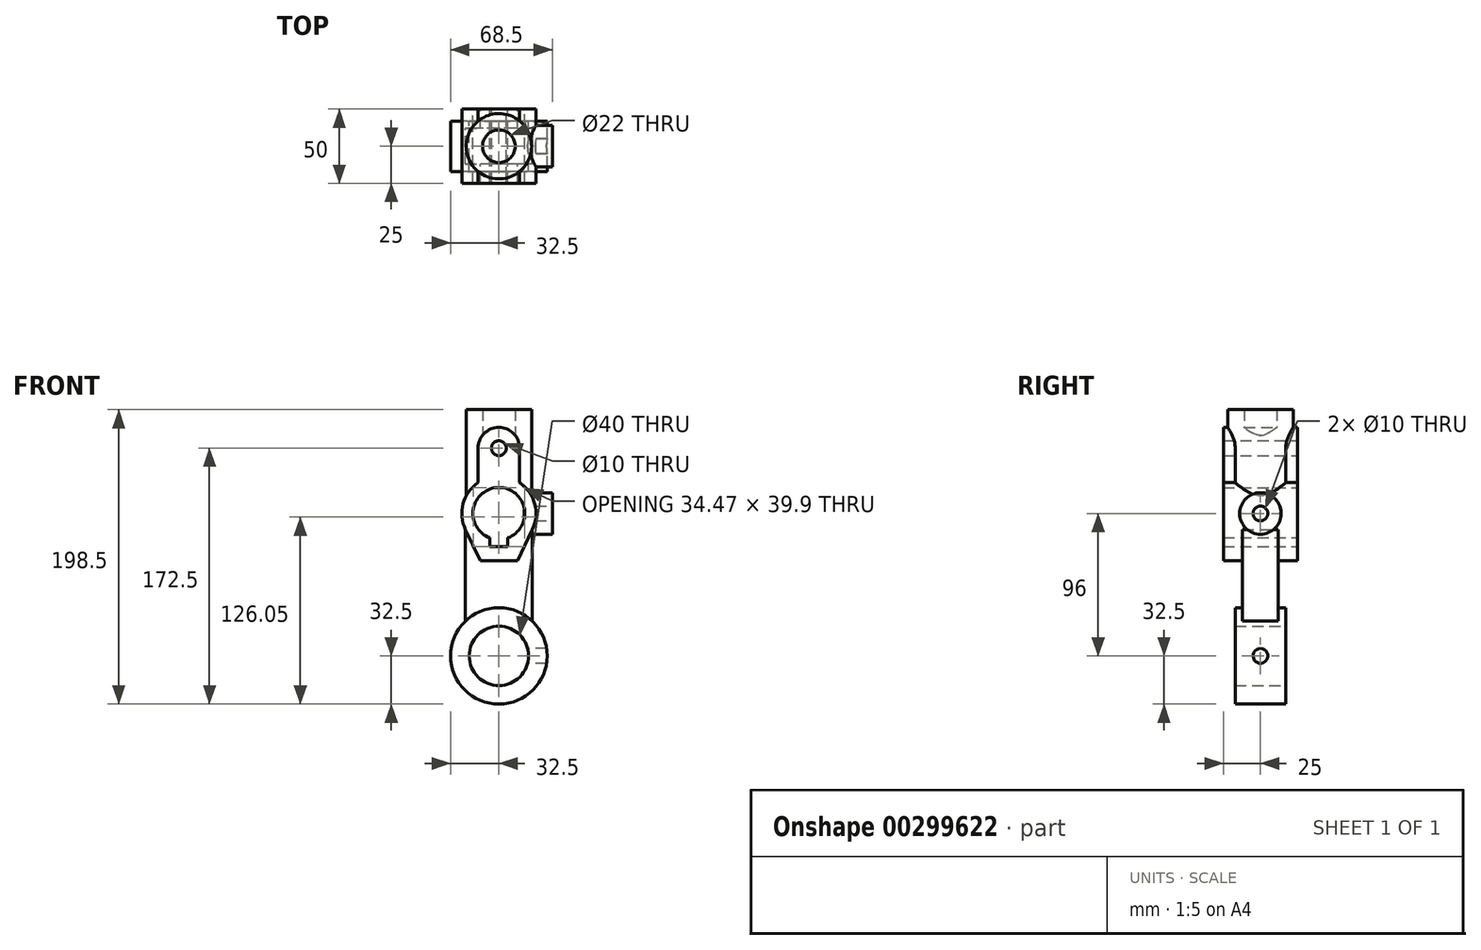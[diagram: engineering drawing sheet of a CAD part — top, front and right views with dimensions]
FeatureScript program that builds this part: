
annotation { "Feature Type Name" : "Feature", "Feature Type Description" : "" }
export const myFeature = defineFeature(function(context is Context, id is Id, definition is map)
    precondition{}
    {
        {
            var Q0;
            Q0=qCreatedBy(makeId("Front.planeOp"),FACE);
            var sketch = newSketch(context, id + "F0", { "sketchPlane" : qUnion([Q0])});
            skCircle(sketch, "E0", {"center": v(0, 0) * mm, "radius": 20 * mm});
            skCircle(sketch, "E1", {"center": v(0, 0) * mm, "radius": 32.5 * mm});
            skSolve(sketch);
        }
        {
            var Q0;
            Q0 = qSketchRegion(id + "F0", true);
            extrude(context, id + "F1", {"entities" : qUnion([Q0]), "endBound" : BoundingType.SYMMETRIC, "depth" : 34 * mm});
        }
        {
            var Q0;
            Q0=qCreatedBy(makeId("Right.planeOp"),FACE);
            var sketch = newSketch(context, id + "F2", { "sketchPlane" : qUnion([Q0])});
            skCircle(sketch, "E2", {"center": v(0, 0) * mm, "radius": 5 * mm});
            skSolve(sketch);
        }
        {
            var Q0;
            Q0 = qSketchRegion(id + "F2", true);
            extrude(context, id + "F3", {"entities" : qUnion([Q0]), "operationType" : NewBodyOperationType.REMOVE, "endBound" : BoundingType.THROUGH_ALL, "depth" : 25 * mm});
        }
        {
            var Q0;
            Q0=qCreatedBy(makeId("Front.planeOp"),FACE);
            var sketch = newSketch(context, id + "F4", { "sketchPlane" : qUnion([Q0])});
            skLineSegment(sketch, "E3", {"start": v(-22.5, 23.45) * mm, "end": v(-22.5, 96) * mm});
            skLineSegment(sketch, "E4", {"start": v(22.5, 23.45) * mm, "end": v(22.5, 96) * mm});
            skLineSegment(sketch, "E5", {"start": v(-22.5, 96) * mm, "end": v(22.5, 96) * mm});
            skArc(sketch, "E6", {"start": v(22.5, 23.45) * mm, "mid": v(0, 32.5) * mm, "end": v(-22.5, 23.45) * mm});
            skSolve(sketch);
        }
        {
            var Q0;
            Q0 = qSketchRegion(id + "F4", true);
            extrude(context, id + "F5", {"entities" : qUnion([Q0]), "operationType" : NewBodyOperationType.ADD, "endBound" : BoundingType.SYMMETRIC, "depth" : 24 * mm});
        }
        {
            var Q0;
            Q0=qCreatedBy(makeId("Front.planeOp"),FACE);
            var sketch = newSketch(context, id + "F6", { "sketchPlane" : qUnion([Q0])});
            skArc(sketch, "E7", {"start": v(6, 79.56) * mm, "mid": v(0, 113.5) * mm, "end": v(-6, 79.56) * mm});
            skLineSegment(sketch, "E8", {"start": v(-6, 79.56) * mm, "end": v(-6, 73.6) * mm});
            skLineSegment(sketch, "E9", {"start": v(-6, 73.6) * mm, "end": v(6, 73.6) * mm});
            skLineSegment(sketch, "E10", {"start": v(6, 73.6) * mm, "end": v(6, 79.56) * mm});
            skLineSegment(sketch, "E11", {"start": v(-12.5, 64) * mm, "end": v(12.5, 64) * mm});
            skCircle(sketch, "E12", {"center": v(0, 140) * mm, "radius": 5 * mm});
            skArc(sketch, "E13", {"start": v(14, 140) * mm, "mid": v(0, 154) * mm, "end": v(-14, 140) * mm});
            skArc(sketch, "E14", {"start": v(-14, 116.71) * mm, "mid": v(-24.14, 102.5) * mm, "end": v(-22.5, 85.1) * mm});
            skLineSegment(sketch, "E15", {"start": v(-14, 140) * mm, "end": v(-14, 116.71) * mm});
            skLineSegment(sketch, "E16", {"start": v(-12.5, 64) * mm, "end": v(-22.5, 85.1) * mm});
            skLineSegment(sketch, "E17.MirrorCS", {"start": v(12.5, 64) * mm, "end": v(22.5, 85.1) * mm});
            skArc(sketch, "E18.MirrorCS", {"start": v(14, 116.71) * mm, "mid": v(24.14, 102.5) * mm, "end": v(22.5, 85.1) * mm});
            skLineSegment(sketch, "E19.MirrorCS", {"start": v(14, 140) * mm, "end": v(14, 116.71) * mm});
            skSolve(sketch);
        }
        {
            var Q0;
            Q0 = qSketchRegion(id + "F6", true);
            extrude(context, id + "F7", {"entities" : qUnion([Q0]), "operationType" : NewBodyOperationType.ADD, "endBound" : BoundingType.SYMMETRIC, "depth" : 50 * mm});
        }
        {
            var Q0;
            {var subQ0=sQuery(id+"F4.wireOp",EDGE,"E5");Q0=makeQuery(id+"F7.boolean.opBoolean","SPLIT",FACE,{"disambiguationData":[TD([makeQuery(id+"F5.opExtrude","SWEPT_FACE",FACE,{"disambiguationData":[OSD([subQ0])]})])],"derivedFrom":makeQuery(id+"F5.opExtrude","CAP_FACE",FACE,{"disambiguationData":[OSD([sQuery(id+"F4.wireOp",EDGE,"E3"),sQuery(id+"F4.wireOp",EDGE,"E4"),subQ0,sQuery(id+"F4.wireOp",EDGE,"E6")])],"isStart":false})});}
            extrude(context, id + "F8", {"entities" : qUnion([Q0]), "operationType" : NewBodyOperationType.REMOVE, "endBound" : BoundingType.THROUGH_ALL, "oppositeDirection" : true, "depth" : 25 * mm});
        }
        {
            var Q0;
            Q0=qCreatedBy(makeId("Top.planeOp"),FACE);
            cPlane(context, id + "F9", {"entities" : qUnion([Q0]), "cplaneType" : CPlaneType.OFFSET, "offset" : 96 * mm, "width" : 150 * mm, "height" : 150 * mm});
        }
        {
            var Q0;
            Q0=qCreatedBy(id+"F9.planeOp",FACE);
            var sketch = newSketch(context, id + "F10", { "sketchPlane" : qUnion([Q0])});
            skCircle(sketch, "E20", {"center": v(0, 0) * mm, "radius": 11 * mm});
            skCircle(sketch, "E21", {"center": v(0, 0) * mm, "radius": 22 * mm});
            skSolve(sketch);
        }
        {
            var Q0;
            Q0 = qSketchRegion(id + "F10", true);
            extrude(context, id + "F11", {"entities" : qUnion([Q0]), "operationType" : NewBodyOperationType.ADD, "depth" : 70 * mm});
        }
        {
            var Q0;
            Q0=makeQuery(id+"F7.opExtrude","CAP_FACE",FACE,{"disambiguationData":[OSD([sQuery(id+"F6.wireOp",EDGE,"E7"),sQuery(id+"F6.wireOp",EDGE,"E8"),sQuery(id+"F6.wireOp",EDGE,"E9"),sQuery(id+"F6.wireOp",EDGE,"E10"),sQuery(id+"F6.wireOp",EDGE,"E11"),sQuery(id+"F6.wireOp",EDGE,"E12"),sQuery(id+"F6.wireOp",EDGE,"E13"),sQuery(id+"F6.wireOp",EDGE,"E14"),sQuery(id+"F6.wireOp",EDGE,"E15"),sQuery(id+"F6.wireOp",EDGE,"E16"),sQuery(id+"F6.wireOp",EDGE,"E17.MirrorCS"),sQuery(id+"F6.wireOp",EDGE,"E18.MirrorCS"),sQuery(id+"F6.wireOp",EDGE,"E19.MirrorCS")])],"isStart":false});
            var sketch = newSketch(context, id + "F12", { "sketchPlane" : qUnion([Q0])});
            skCircle(sketch, "E22", {"center": v(0, 96) * mm, "radius": 17.5 * mm});
            skCircle(sketch, "E23", {"center": v(0, 140) * mm, "radius": 5 * mm});
            skSolve(sketch);
        }
        {
            var Q0;
            Q0 = qSketchRegion(id + "F12", true);
            extrude(context, id + "F13", {"entities" : qUnion([Q0]), "operationType" : NewBodyOperationType.REMOVE, "endBound" : BoundingType.THROUGH_ALL, "oppositeDirection" : true, "depth" : 25 * mm});
        }
        {
            var Q0;
            Q0=qCreatedBy(makeId("Right.planeOp"),FACE);
            cPlane(context, id + "F14", {"entities" : qUnion([Q0]), "cplaneType" : CPlaneType.OFFSET, "offset" : 36 * mm, "width" : 150 * mm, "height" : 150 * mm});
        }
        {
            var Q0;
            Q0=qCreatedBy(id+"F14.planeOp",FACE);
            var sketch = newSketch(context, id + "F15", { "sketchPlane" : qUnion([Q0])});
            skCircle(sketch, "E24", {"center": v(0, 96) * mm, "radius": 14 * mm});
            skCircle(sketch, "E25", {"center": v(0, 96) * mm, "radius": 5 * mm});
            skSolve(sketch);
        }
        {
            var Q0;
            Q0 = qSketchRegion(id + "F15", true);
            var Q1;
            {var subQ0=sQuery(id+"F10.wireOp",EDGE,"E21");Q1=makeQuery(id+"F11.boolean.opBoolean","SPLIT",FACE,{"disambiguationData":[TD([makeQuery(id+"F7.opExtrude","SWEPT_FACE",FACE,{"disambiguationData":[OSD([sQuery(id+"F6.wireOp",EDGE,"E13")])]}),makeQuery(id+"F7.opExtrude","SWEPT_FACE",FACE,{"disambiguationData":[OSD([sQuery(id+"F6.wireOp",EDGE,"E14")])]}),makeQuery(id+"F7.opExtrude","SWEPT_FACE",FACE,{"disambiguationData":[OSD([sQuery(id+"F6.wireOp",EDGE,"E15")])]}),makeQuery(id+"F7.opExtrude","SWEPT_FACE",FACE,{"disambiguationData":[OSD([sQuery(id+"F6.wireOp",EDGE,"E18.MirrorCS")])]}),makeQuery(id+"F7.opExtrude","SWEPT_FACE",FACE,{"disambiguationData":[OSD([sQuery(id+"F6.wireOp",EDGE,"E19.MirrorCS")])]}),makeQuery(id+"F11.opExtrude","CAP_FACE",FACE,{"disambiguationData":[OSD([sQuery(id+"F10.wireOp",EDGE,"E20"),subQ0])],"isStart":false})])],"derivedFrom":makeQuery(id+"F11.opExtrude","SWEPT_FACE",FACE,{"disambiguationData":[OSD([subQ0])]})});}
            extrude(context, id + "F16", {"entities" : qUnion([Q0]), "operationType" : NewBodyOperationType.ADD, "endBound" : BoundingType.UP_TO_SURFACE, "oppositeDirection" : true, "endBoundEntityFace" : qUnion([Q1]), "depth" : 25 * mm});
        }
    });
